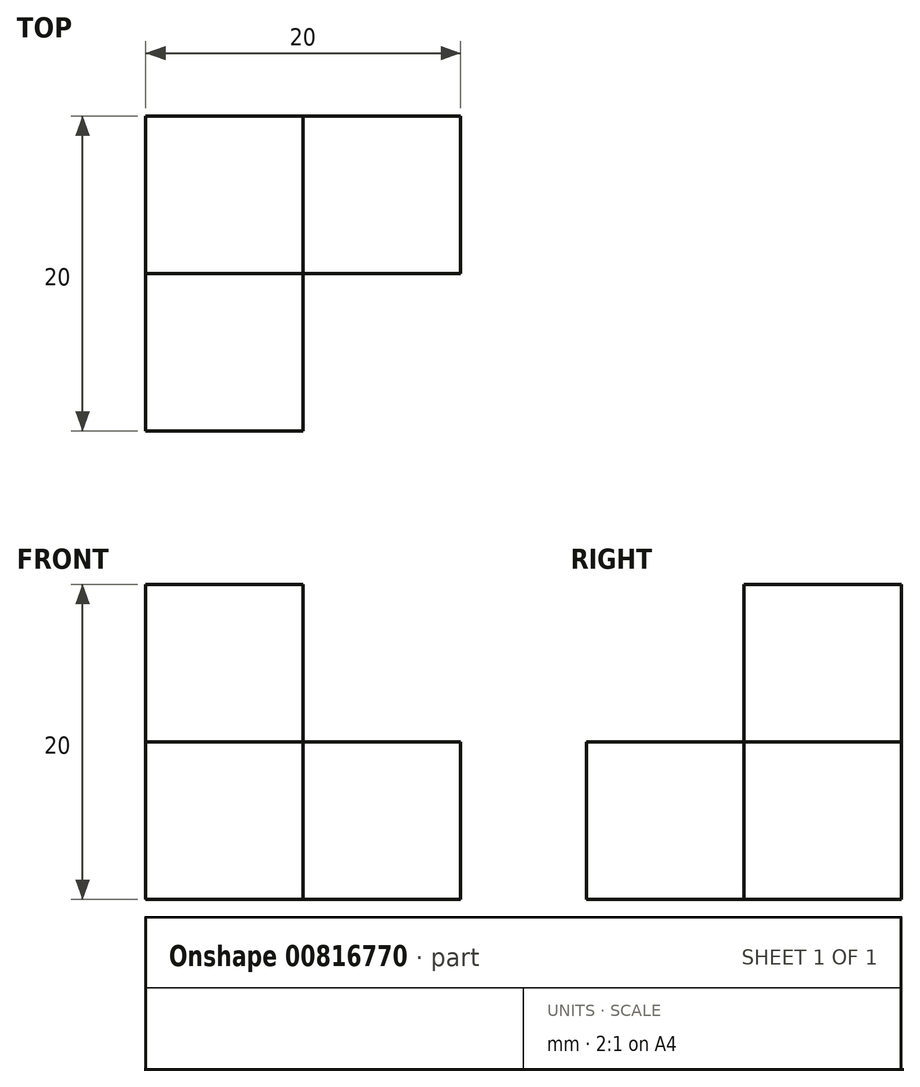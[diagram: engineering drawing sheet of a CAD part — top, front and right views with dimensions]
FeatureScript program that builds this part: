
annotation { "Feature Type Name" : "Feature", "Feature Type Description" : "" }
export const myFeature = defineFeature(function(context is Context, id is Id, definition is map)
    precondition{}
    {
        {
            var Q0;
            Q0=qCreatedBy(makeId("Top.planeOp"),FACE);
            var sketch = newSketch(context, id + "F0", { "sketchPlane" : qUnion([Q0])});
            skLineSegment(sketch, "E0.bottom", {"start": v(0, 0) * mm, "end": v(10, 0) * mm});
            skLineSegment(sketch, "E0.top", {"start": v(0, 10) * mm, "end": v(10, 10) * mm});
            skLineSegment(sketch, "E0.left", {"start": v(0, 0) * mm, "end": v(0, 10) * mm});
            skLineSegment(sketch, "E0.right", {"start": v(10, 0) * mm, "end": v(10, 10) * mm});
            skSolve(sketch);
        }
        {
            var Q0;
            Q0 = qSketchRegion(id + "F0", true);
            extrude(context, id + "F1", {"entities" : qUnion([Q0]), "depth" : 20 * mm, "offsetDistance" : 25 * mm});
        }
        {
            var Q0;
            Q0=makeQuery(id+"F1.opExtrude","SWEPT_FACE",FACE,{"disambiguationData":[OSD([sQuery(id+"F0.wireOp",EDGE,"E0.bottom")])]});
            var sketch = newSketch(context, id + "F2", { "sketchPlane" : qUnion([Q0])});
            skLineSegment(sketch, "E1.bottom", {"start": v(0, 0) * mm, "end": v(10, 0) * mm});
            skLineSegment(sketch, "E1.top", {"start": v(0, 10) * mm, "end": v(10, 10) * mm});
            skLineSegment(sketch, "E1.left", {"start": v(0, 0) * mm, "end": v(0, 10) * mm});
            skLineSegment(sketch, "E1.right", {"start": v(10, 0) * mm, "end": v(10, 10) * mm});
            skSolve(sketch);
        }
        {
            var Q0;
            Q0=makeQuery(id+"F2.imprint","IMPRINT",FACE,{"disambiguationData":[TD([[makeQuery(id+"F2.imprint","IMPRINT",EDGE,{"derivedFrom":sQuery(id+"F2.wireOp",EDGE,"E1.bottom")}),1.0]])]});
            extrude(context, id + "F3", {"entities" : qUnion([Q0]), "operationType" : NewBodyOperationType.ADD, "depth" : 10 * mm, "offsetDistance" : 25 * mm});
        }
        {
            var Q0;
            Q0=makeQuery(id+"F3.boolean.opBoolean","MERGE",FACE,{"derivedFrom":[makeQuery(id+"F1.opExtrude","SWEPT_FACE",FACE,{"disambiguationData":[OSD([sQuery(id+"F0.wireOp",EDGE,"E0.right")])]}),makeQuery(id+"F3.opExtrude","SWEPT_FACE",FACE,{"disambiguationData":[OSD([sQuery(id+"F2.wireOp",EDGE,"E1.right")])]})]});
            var sketch = newSketch(context, id + "F4", { "sketchPlane" : qUnion([Q0])});
            skLineSegment(sketch, "E2.bottom", {"start": v(0, 0) * mm, "end": v(10, 0) * mm});
            skLineSegment(sketch, "E2.top", {"start": v(0, 10) * mm, "end": v(10, 10) * mm});
            skLineSegment(sketch, "E2.left", {"start": v(0, 0) * mm, "end": v(0, 10) * mm});
            skLineSegment(sketch, "E2.right", {"start": v(10, 0) * mm, "end": v(10, 10) * mm});
            skSolve(sketch);
        }
        {
            var Q0;
            Q0 = qSketchRegion(id + "F4", true);
            extrude(context, id + "F5", {"entities" : qUnion([Q0]), "operationType" : NewBodyOperationType.ADD, "depth" : 10 * mm, "offsetDistance" : 25 * mm});
        }
    });
